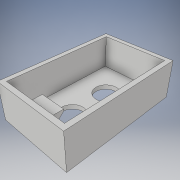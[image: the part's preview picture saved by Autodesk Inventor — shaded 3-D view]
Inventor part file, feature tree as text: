
AUTODESK INVENTOR PART (.ipt)
format: ipt  version: 2019 (Build 230136000, 136)  size: 235,520 bytes
history: native  units: mm
features: sketch x11, projected_geometry x11, extrude x10, chamfer x4
ambient origin geometry x8: Origin, YZ Plane, XZ Plane, XY Plane, X Axis, Y Axis, Z Axis, Center Point
bodies: Solid1 (feature_tree)
feature tree (36):
  extrude  "Extrusion1"  Depth=16.1mm
  extrude  "Extrusion8"  Depth=29.0mm
  extrude  "Extrusion9"  Depth=14.5mm
  extrude  "Extrusion10"  Depth=14.25mm
  chamfer  "Chamfer4"  Distance=3.0mm
  extrude  "Extrusion2"  Depth=23.0mm
  extrude  "Extrusion3"  Depth=51.0mm
  extrude  "Extrusion4"  Depth=3.0mm
  extrude  "Extrusion5"  Depth=15.0mm TaperAngle=0.0deg
  chamfer  "Chamfer1"  Distance=4.0mm
  chamfer  "Chamfer2"  Distance=4.0mm
  extrude  "Extrusion6"  Depth=20.0mm
  extrude  "Extrusion7"  Depth=10.0mm TaperAngle=0.0deg
  chamfer  "Chamfer3"  Distance=2.0mm Angle=45.0deg
  sketch  "Sketch8"  dims[d16=3.0mm d17=0.0mm d18=45.0mm]
  sketch  "Sketch1"  dims[d0=16.1mm d1=16.1mm]
  sketch  "Sketch2"  dims[d2=25.5mm d3=29.0mm]
  sketch  "Sketch3"  dims[d4=54.0mm d5=14.5mm]
  sketch  "Sketch4"  dims[d6=14.5mm d7=14.25mm]
  sketch  "Sketch5"  dims[d8=14.25mm d9=3.0mm d10=0.0mm]
  projected_geometry  "Projected Loop1"
  projected_geometry  "Projected Loop2"
  projected_geometry  "Projected Loop3"
  projected_geometry  "Projected Loop4"
  sketch  "Sketch6"  dims[d11=23.0mm d12=48.0mm]
  projected_geometry  "Projected Loop5"
  projected_geometry  "Projected Loop6"
  sketch  "Sketch7"  dims[d13=25.0mm d14=0.0mm d15=51.0mm]
  projected_geometry  "Projected Loop7"
  projected_geometry  "Projected Loop8"
  sketch  "Sketch9"  dims[d19=48.0mm d20=15.0mm d21=0.0mm]
  projected_geometry  "Projected Loop9"
  sketch  "Sketch10"  dims[d22=3.5mm]
  projected_geometry  "Projected Loop10"
  sketch  "Sketch11"  dims[d23=4.0mm d24=4.0mm d25=4.0mm d26=20.0mm d28=40.0mm d29=20.0mm d31=37.0mm d34=10.0mm d35=0.0mm d36=2.0mm d37=2.0mm d38=45.0deg d39=2.0mm d40=2.0mm d41=45.0deg d42=6.0mm d43=20.0mm d45=40.0mm d46=20.0mm d48=37.0mm d51=10.0mm d52=0.0mm d53=4.0mm d54=15.0mm d55=3.0mm d56=18.0mm d57=18.0mm d58=16.0mm d59=0.0mm d60=2.0mm d61=2.0mm d62=45.0deg d63=6.0mm d64=46.0mm d65=73.0mm d66=3.0mm d67=0.0mm d68=3.0mm d69=3.0mm d70=3.0mm d71=3.0mm d72=20.0mm d73=0.0mm d74=15.0mm d75=1.0mm d76=12.5mm d77=12.5mm d78=1.0mm d79=6.0mm d80=10.0mm d81=0.0mm d82=10.0mm d83=2.0mm d84=45.0deg]
  projected_geometry  "Projected Loop11"
